# Revit family: Cooktop
name_source: partatom
category: Modelos genéricos
units: mm (PartAtom-declared; Revit-internal decimal feet)

## family parameters
Com base no plano de trabalho = Não
Compartilhado = Não
Corte com vazios quando carregada = Não
Cota do conector redondo = Utilizar diâmetro
Pode hospedar o vergalhão = Não
Ponto de cálculo do ambiente = Não
Sempre na vertical = Sim
Tipo de parte = Normal

## types (1)
- Cooktop
    Descrição = Cooktop por indução
    Dimensões = 900 x 350 x 59 mm (Profundidade)
    Elevação padrão = 0 mm  [stored 0 ft]
    Fabricante = Tramontina
    Frequência = 50 - 60 Hz
    Indicador de calor residual = Sim
    Itens inclusos = Espátula
    Material predominante = Superfície vitrocerâmica
    Modelo = Cooptop Slim Bridge 4EI 90
    Modo booster = Sim, nas duas áreas
    Modo bridge = Sim
    Níveis de temperatura = 9
    Potência das áreas = 2x 1,9 kW + 2x 2,6 kW
    Potência total = 9 kW
    Referência do produto = 94722/222
    Tensão = 220 V
    URL da ficha técnica = https://assets.tramontina.com.br
    URL do fabricante = tramontina.com.br
    URL do produto = https://www.tramontina.com.br
    URL dos arquivos BIM = tramontina.com.br/biblioteca

note: [stored X ft] marks values corroborated as IEEE doubles in the binary element streams (Revit-internal decimal feet)
